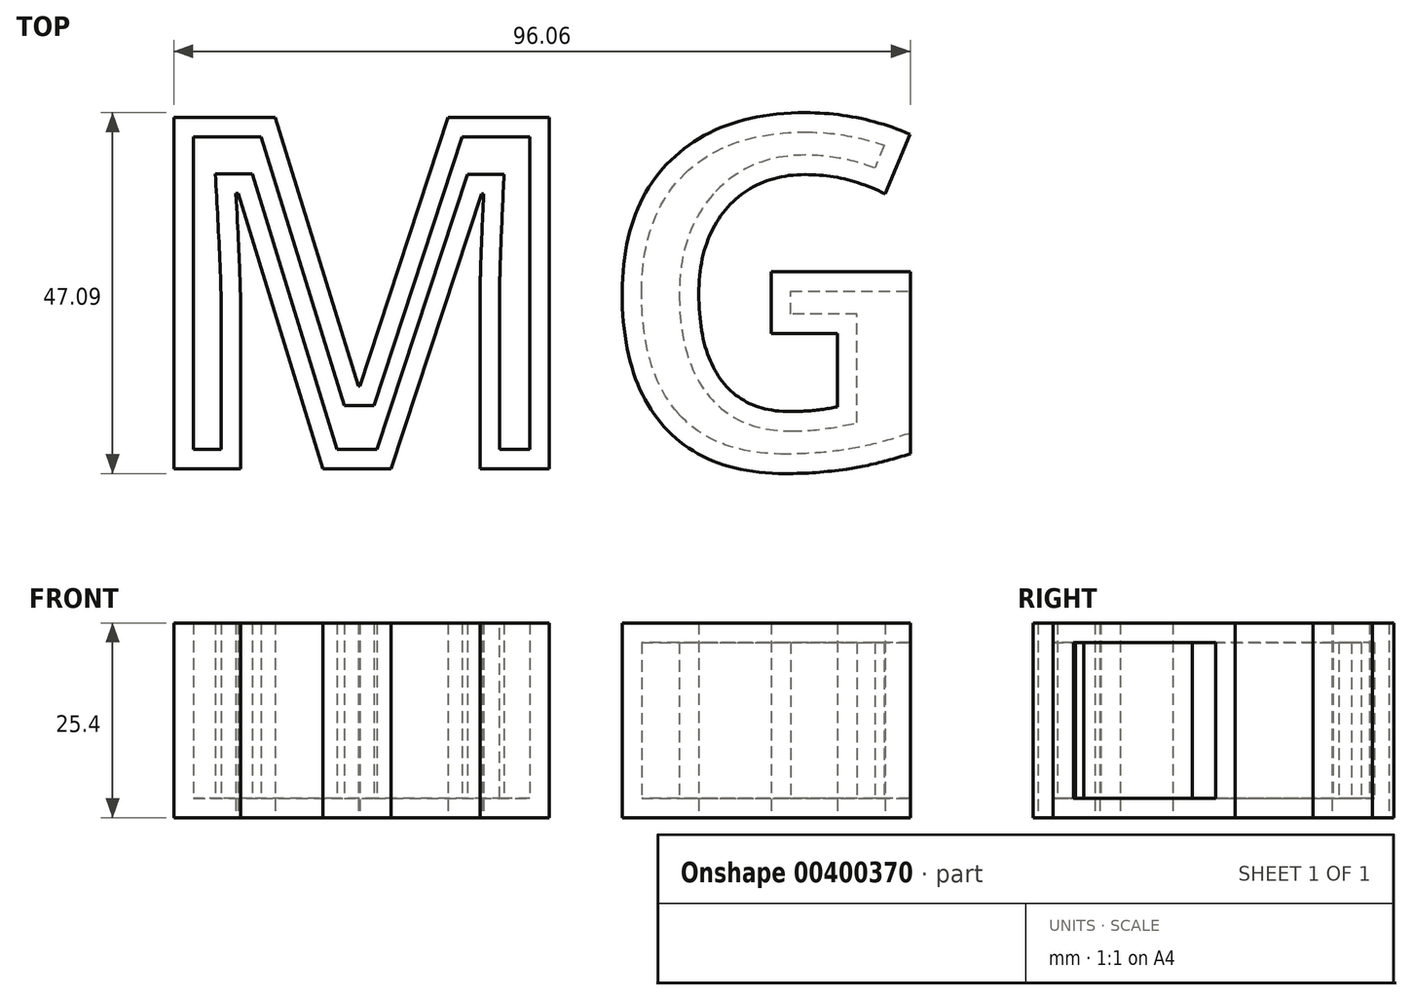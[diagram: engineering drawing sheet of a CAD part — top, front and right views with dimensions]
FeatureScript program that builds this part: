
annotation { "Feature Type Name" : "Feature", "Feature Type Description" : "" }
export const myFeature = defineFeature(function(context is Context, id is Id, definition is map)
    precondition{}
    {
        {
            var Q0;
            Q0=qCreatedBy(makeId("Top.planeOp"),FACE);
            var sketch = newSketch(context, id + "F0", { "sketchPlane" : qUnion([Q0])});
            skText(sketch, "E0", { "text": "MG", "fontName": "OpenSans-Bold.ttf"});
            const initialGuessF0  = {"E0": [-0.0354, -0.0462, 1, 0, 0.0462]};
            skSetInitialGuess(sketch, initialGuessF0);
            skSolve(sketch);
        }
        {
            var Q0;
            Q0 = qSketchRegion(id + "F0", true);
            extrude(context, id + "F1", {"entities" : qUnion([Q0]), "depth" : 25.4 * mm});
        }
        {
            var Q0;
            Q0=makeQuery(id+"F1.opExtrude","CAP_FACE",FACE,{"disambiguationData":[OSD([sQuery(id+"F0.wireOp",EDGE,"E0.sketch_text.stroke-0"),sQuery(id+"F0.wireOp",EDGE,"E0.sketch_text.stroke-1"),sQuery(id+"F0.wireOp",EDGE,"E0.sketch_text.stroke-2"),sQuery(id+"F0.wireOp",EDGE,"E0.sketch_text.stroke-3"),sQuery(id+"F0.wireOp",EDGE,"E0.sketch_text.stroke-4"),sQuery(id+"F0.wireOp",EDGE,"E0.sketch_text.stroke-5"),sQuery(id+"F0.wireOp",EDGE,"E0.sketch_text.stroke-6"),sQuery(id+"F0.wireOp",EDGE,"E0.sketch_text.stroke-7"),sQuery(id+"F0.wireOp",EDGE,"E0.sketch_text.stroke-8"),sQuery(id+"F0.wireOp",EDGE,"E0.sketch_text.stroke-9"),sQuery(id+"F0.wireOp",EDGE,"E0.sketch_text.stroke-10"),sQuery(id+"F0.wireOp",EDGE,"E0.sketch_text.stroke-11"),sQuery(id+"F0.wireOp",EDGE,"E0.sketch_text.stroke-12"),sQuery(id+"F0.wireOp",EDGE,"E0.sketch_text.stroke-13"),sQuery(id+"F0.wireOp",EDGE,"E0.sketch_text.stroke-14"),sQuery(id+"F0.wireOp",EDGE,"E0.sketch_text.stroke-15"),sQuery(id+"F0.wireOp",EDGE,"E0.sketch_text.stroke-16"),sQuery(id+"F0.wireOp",EDGE,"E0.sketch_text.stroke-17"),sQuery(id+"F0.wireOp",EDGE,"E0.sketch_text.stroke-18")])],"isStart":false});
            shell(context, id + "F2", {"entities" : qUnion([Q0]), "thickness" : 2.54 * mm});
        }
        {
            var Q0;
            Q0=makeQuery(id+"F1.opExtrude","SWEPT_FACE",FACE,{"disambiguationData":[OSD([sQuery(id+"F0.wireOp",EDGE,"E0.sketch_text.stroke-20")])]});
            shell(context, id + "F3", {"entities" : qUnion([Q0]), "thickness" : 2.54 * mm});
        }
    });
